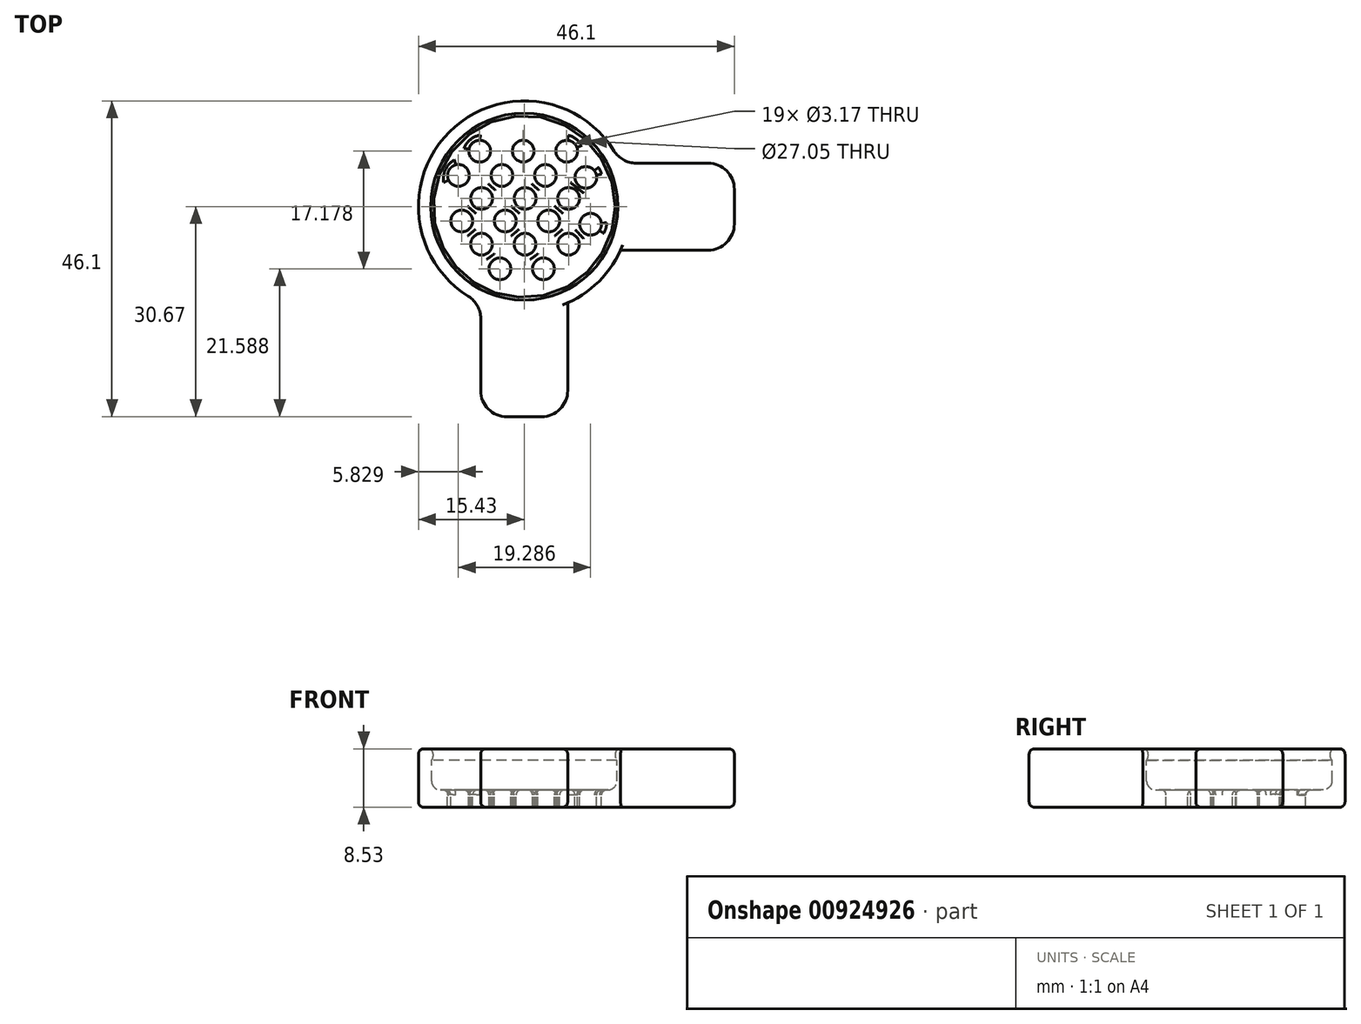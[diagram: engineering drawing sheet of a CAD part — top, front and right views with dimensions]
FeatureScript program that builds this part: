
annotation { "Feature Type Name" : "Feature", "Feature Type Description" : "" }
export const myFeature = defineFeature(function(context is Context, id is Id, definition is map)
    precondition{}
    {
        {
            var Q0;
            Q0=qCreatedBy(makeId("Front.planeOp"),FACE);
            var sketch = newSketch(context, id + "F0", { "sketchPlane" : qUnion([Q0])});
            skLineSegment(sketch, "E0", {"start": v(15.43, 6.71) * mm, "end": v(15.43, 0) * mm});
            skLineSegment(sketch, "E1", {"start": v(15.43, 0) * mm, "end": v(0, 0) * mm});
            skArc(sketch, "E2", {"start": v(15.43, 6.71) * mm, "mid": v(13.63, 6.73) * mm, "end": v(13.65, 8.53) * mm});
            skLineSegment(sketch, "E3", {"start": v(0, 10.9) * mm, "end": v(0, -2.45) * mm, "construction": true});
            skLineSegment(sketch, "E4", {"start": v(0, 0) * mm, "end": v(0, 2.54) * mm});
            skLineSegment(sketch, "E5", {"start": v(0, 2.54) * mm, "end": v(12.26, 2.54) * mm});
            skLineSegment(sketch, "E6", {"start": v(13.53, 3.81) * mm, "end": v(13.53, 6.86) * mm});
            skLineSegment(sketch, "E7", {"start": v(15.43, 6.71) * mm, "end": v(15.43, 8.53) * mm});
            skLineSegment(sketch, "E8", {"start": v(15.43, 8.53) * mm, "end": v(13.65, 8.53) * mm});
            skPoint(sketch, "E9.visualSharp", {"position": v(13.53, 2.54) * mm});
            skArc(sketch, "E10.filletArc", {"start": v(12.26, 2.54) * mm, "mid": v(13.15, 2.91) * mm, "end": v(13.53, 3.81) * mm});
            skPoint(sketch, "E11.visualSharp", {"position": v(15.43, 0) * mm});
            skPoint(sketch, "E12.visualSharp", {"position": v(15.43, 8.53) * mm});
            skSolve(sketch);
        }
        {
            var Q0;
            Q0=qSketchRegion(id+"F0",true);
            var Q1;
            Q1=sQuery(id+"F0.wireOp",EDGE,"E3");
            revolve(context, id + "F1", {"surfaceOperationType" : NewSurfaceOperationType.NEW, "entities" : qUnion([Q0]), "axis" : qUnion([Q1]), "revolveType" : RevolveType.FULL});
        }
        {
            var Q0;
            Q0=makeQuery(id+"F1.opRevolve","SWEPT_FACE",FACE,{"disambiguationData":[OSD([sQuery(id+"F0.wireOp",EDGE,"E8")])]});
            var sketch = newSketch(context, id + "F2", { "sketchPlane" : qUnion([Q0])});
            skLineSegment(sketch, "E13.bottom", {"start": v(30.67, 6.35) * mm, "end": v(14.06, 6.35) * mm});
            skLineSegment(sketch, "E13.top", {"start": v(30.67, -6.35) * mm, "end": v(14.06, -6.35) * mm});
            skLineSegment(sketch, "E13.left", {"start": v(30.67, 6.35) * mm, "end": v(30.67, -6.35) * mm});
            skLineSegment(sketch, "E14.bottom", {"start": v(6.35, -30.67) * mm, "end": v(-6.35, -30.67) * mm});
            skLineSegment(sketch, "E14.left", {"start": v(6.35, -30.67) * mm, "end": v(6.35, -14.06) * mm});
            skLineSegment(sketch, "E14.right", {"start": v(-6.35, -30.67) * mm, "end": v(-6.35, -14.06) * mm});
            skArc(sketch, "E15.0", {"start": v(-6.35, -14.06) * mm, "mid": v(0, -15.43) * mm, "end": v(6.35, -14.06) * mm});
            skArc(sketch, "E16.trimOffspring", {"start": v(14.06, -6.35) * mm, "mid": v(15.43, 0) * mm, "end": v(14.06, 6.35) * mm});
            skSolve(sketch);
        }
        {
            var Q0;
            Q0=qSketchRegion(id+"F2",true);
            var Q1;
            Q1=makeQuery(id+"F1.opRevolve","SWEPT_FACE",FACE,{"disambiguationData":[OSD([sQuery(id+"F0.wireOp",EDGE,"E1")])]});
            extrude(context, id + "F3", {"entities" : qUnion([Q0]), "operationType" : NewBodyOperationType.ADD, "endBound" : BoundingType.UP_TO_SURFACE, "oppositeDirection" : true, "depth" : 25.4 * mm, "endBoundEntityFace" : qUnion([Q1]), "offsetDistance" : 25.4 * mm});
        }
        {
            var Q0;
            Q0=makeQuery(id+"F3.opExtrude","SWEPT_EDGE",EDGE,{"disambiguationData":[OSD([sQuery(id+"F2.wireOp",EDGE,"E14.bottom"),sQuery(id+"F2.wireOp",EDGE,"E14.right")])]});
            var Q1;
            Q1=makeQuery(id+"F3.opExtrude","SWEPT_EDGE",EDGE,{"disambiguationData":[OSD([sQuery(id+"F0.wireOp",EDGE,"E7"),sQuery(id+"F0.wireOp",EDGE,"E8"),sQuery(id+"F2.wireOp",EDGE,"E14.right"),sQuery(id+"F2.wireOp",EDGE,"E15.0")])]});
            var Q2;
            Q2=makeQuery(id+"F3.opExtrude","SWEPT_EDGE",EDGE,{"disambiguationData":[OSD([sQuery(id+"F2.wireOp",EDGE,"E14.bottom"),sQuery(id+"F2.wireOp",EDGE,"E14.left")])]});
            var Q3;
            Q3=makeQuery(id+"F3.opExtrude","SWEPT_EDGE",EDGE,{"disambiguationData":[OSD([sQuery(id+"F0.wireOp",EDGE,"E7"),sQuery(id+"F0.wireOp",EDGE,"E8"),sQuery(id+"F2.wireOp",EDGE,"E14.left"),sQuery(id+"F2.wireOp",EDGE,"E15.0")])]});
            var Q4;
            Q4=makeQuery(id+"F3.opExtrude","SWEPT_EDGE",EDGE,{"disambiguationData":[OSD([sQuery(id+"F0.wireOp",EDGE,"E7"),sQuery(id+"F0.wireOp",EDGE,"E8"),sQuery(id+"F2.wireOp",EDGE,"E13.top"),sQuery(id+"F2.wireOp",EDGE,"E16.trimOffspring")])]});
            var Q5;
            Q5=makeQuery(id+"F3.opExtrude","SWEPT_EDGE",EDGE,{"disambiguationData":[OSD([sQuery(id+"F2.wireOp",EDGE,"E13.top"),sQuery(id+"F2.wireOp",EDGE,"E13.left")])]});
            var Q6;
            Q6=makeQuery(id+"F3.opExtrude","SWEPT_EDGE",EDGE,{"disambiguationData":[OSD([sQuery(id+"F2.wireOp",EDGE,"E13.bottom"),sQuery(id+"F2.wireOp",EDGE,"E13.left")])]});
            var Q7;
            Q7=makeQuery(id+"F3.opExtrude","SWEPT_EDGE",EDGE,{"disambiguationData":[OSD([sQuery(id+"F0.wireOp",EDGE,"E7"),sQuery(id+"F0.wireOp",EDGE,"E8"),sQuery(id+"F2.wireOp",EDGE,"E13.bottom"),sQuery(id+"F2.wireOp",EDGE,"E16.trimOffspring")])]});
            fillet(context, id + "F4", {"entities" : qUnion([Q0, Q1, Q2, Q3, Q4, Q5, Q6, Q7]), "radius" : 3.8 * mm, "tangentPropagation" : true, "allowEdgeOverflow" : false});
        }
        {
            var Q0;
            Q0=makeQuery(id+"F3.opExtrude","CAP_EDGE",EDGE,{"disambiguationData":[OSD([sQuery(id+"F2.wireOp",EDGE,"E14.bottom")])],"isStart":true});
            var Q1;
            Q1=makeQuery(id+"F3.opExtrude","CAP_EDGE",EDGE,{"disambiguationData":[OSD([sQuery(id+"F2.wireOp",EDGE,"E14.bottom")])],"isStart":false});
            fillet(context, id + "F5", {"entities" : qUnion([Q0, Q1]), "radius" : 0.76 * mm, "tangentPropagation" : true, "allowEdgeOverflow" : false});
        }
        {
            var Q0;
            Q0=makeQuery(id+"F1.opRevolve","SWEPT_FACE",FACE,{"disambiguationData":[OSD([sQuery(id+"F0.wireOp",EDGE,"E5")])]});
            var sketch = newSketch(context, id + "F6", { "sketchPlane" : qUnion([Q0])});
            skCircle(sketch, "E17", {"center": v(-6.7, 7.93) * mm, "radius": 1.4 * mm});
            skCircle(sketch, "E18.1.0.0", {"center": v(-2.25, 7.93) * mm, "radius": 1.4 * mm});
            skCircle(sketch, "E18.2.0.0", {"center": v(2.2, 7.93) * mm, "radius": 1.4 * mm});
            skCircle(sketch, "E18.3.0.0", {"center": v(6.64, 7.93) * mm, "radius": 1.4 * mm});
            skLineSegment(sketch, "E18.direction1", {"start": v(-6.7, 7.93) * mm, "end": v(-2.25, 7.93) * mm, "construction": true});
            skCircle(sketch, "E19", {"center": v(-8.66, 4.6) * mm, "radius": 1.4 * mm});
            skCircle(sketch, "E20.1.0.0", {"center": v(-4.22, 4.6) * mm, "radius": 1.4 * mm});
            skCircle(sketch, "E20.2.0.0", {"center": v(0.23, 4.6) * mm, "radius": 1.4 * mm});
            skCircle(sketch, "E20.3.0.0", {"center": v(4.67, 4.6) * mm, "radius": 1.4 * mm});
            skLineSegment(sketch, "E20.direction1", {"start": v(-8.66, 4.6) * mm, "end": v(-4.22, 4.6) * mm, "construction": true});
            skCircle(sketch, "E21.3.0.0", {"center": v(8.32, 4.74) * mm, "radius": 1.34 * mm});
            skCircle(sketch, "E22", {"center": v(-6.88, 1.46) * mm, "radius": 1.4 * mm});
            skCircle(sketch, "E23.1.0.0", {"center": v(-2.44, 1.46) * mm, "radius": 1.4 * mm});
            skCircle(sketch, "E23.2.0.0", {"center": v(2, 1.46) * mm, "radius": 1.4 * mm});
            skCircle(sketch, "E23.3.0.0", {"center": v(6.45, 1.46) * mm, "radius": 1.4 * mm});
            skLineSegment(sketch, "E23.direction1", {"start": v(-6.88, 1.46) * mm, "end": v(-2.44, 1.46) * mm, "construction": true});
            skCircle(sketch, "E24", {"center": v(-8.85, -1.87) * mm, "radius": 1.4 * mm});
            skCircle(sketch, "E25.1.0.0", {"center": v(-4.4, -1.87) * mm, "radius": 1.4 * mm});
            skCircle(sketch, "E25.2.0.0", {"center": v(0.04, -1.87) * mm, "radius": 1.4 * mm});
            skCircle(sketch, "E25.3.0.0", {"center": v(4.49, -1.87) * mm, "radius": 1.4 * mm});
            skLineSegment(sketch, "E25.direction1", {"start": v(-8.85, -1.87) * mm, "end": v(-4.4, -1.87) * mm, "construction": true});
            skCircle(sketch, "E26.3.0.0", {"center": v(8.13, -1.73) * mm, "radius": 1.34 * mm});
            skCircle(sketch, "E27", {"center": v(-6.6, -4.9) * mm, "radius": 1.4 * mm});
            skCircle(sketch, "E28.1.0.0", {"center": v(-2.16, -4.9) * mm, "radius": 1.4 * mm});
            skCircle(sketch, "E28.2.0.0", {"center": v(2.29, -4.9) * mm, "radius": 1.4 * mm});
            skCircle(sketch, "E28.3.0.0", {"center": v(6.73, -4.9) * mm, "radius": 1.4 * mm});
            skLineSegment(sketch, "E28.direction1", {"start": v(-6.6, -4.9) * mm, "end": v(-2.16, -4.9) * mm, "construction": true});
            skCircle(sketch, "E29", {"center": v(-4.25, -8.22) * mm, "radius": 1.4 * mm});
            skCircle(sketch, "E30.1.0.0", {"center": v(0.2, -8.22) * mm, "radius": 1.4 * mm});
            skCircle(sketch, "E30.2.0.0", {"center": v(4.64, -8.22) * mm, "radius": 1.4 * mm});
            skLineSegment(sketch, "E30.direction1", {"start": v(-4.25, -8.22) * mm, "end": v(0.2, -8.22) * mm, "construction": true});
            skSolve(sketch);
        }
        {
            var Q0;
            Q0=makeQuery(id+"F6.imprint","IMPRINT",FACE,{"disambiguationData":[TD([[makeQuery(id+"F6.imprint","IMPRINT",EDGE,{"derivedFrom":sQuery(id+"F6.wireOp",EDGE,"E17")}),-1.0]])]});
            var sketch = newSketch(context, id + "F7", { "sketchPlane" : qUnion([Q0])});
            skCircle(sketch, "E31", {"center": v(-6.5, 8.1) * mm, "radius": 1.59 * mm});
            skCircle(sketch, "E32.1.0.0", {"center": v(-0.14, 8.1) * mm, "radius": 1.59 * mm});
            skCircle(sketch, "E32.2.0.0", {"center": v(6.2, 8.1) * mm, "radius": 1.59 * mm});
            skLineSegment(sketch, "E32.direction1", {"start": v(-6.5, 8.1) * mm, "end": v(-0.14, 8.1) * mm, "construction": true});
            skCircle(sketch, "E33", {"center": v(-9.6, 4.55) * mm, "radius": 1.59 * mm});
            skCircle(sketch, "E34.1.0.0", {"center": v(-3.25, 4.55) * mm, "radius": 1.59 * mm});
            skCircle(sketch, "E34.2.0.0", {"center": v(3.1, 4.55) * mm, "radius": 1.59 * mm});
            skLineSegment(sketch, "E34.direction1", {"start": v(-9.6, 4.55) * mm, "end": v(-3.25, 4.55) * mm, "construction": true});
            skCircle(sketch, "E35", {"center": v(-6.22, 1.2) * mm, "radius": 1.59 * mm});
            skCircle(sketch, "E36.1.0.0", {"center": v(0.13, 1.2) * mm, "radius": 1.59 * mm});
            skCircle(sketch, "E36.2.0.0", {"center": v(6.48, 1.2) * mm, "radius": 1.59 * mm});
            skLineSegment(sketch, "E36.direction1", {"start": v(-6.22, 1.2) * mm, "end": v(0.13, 1.2) * mm, "construction": true});
            skCircle(sketch, "E37", {"center": v(-9.12, -2.1) * mm, "radius": 1.59 * mm});
            skCircle(sketch, "E38.1.0.0", {"center": v(-2.77, -2.1) * mm, "radius": 1.59 * mm});
            skCircle(sketch, "E38.2.0.0", {"center": v(3.58, -2.1) * mm, "radius": 1.59 * mm});
            skLineSegment(sketch, "E38.direction1", {"start": v(-9.12, -2.1) * mm, "end": v(-2.77, -2.1) * mm, "construction": true});
            skCircle(sketch, "E39", {"center": v(-6.24, -5.49) * mm, "radius": 1.59 * mm});
            skCircle(sketch, "E40.1.0.0", {"center": v(0.11, -5.49) * mm, "radius": 1.59 * mm});
            skCircle(sketch, "E40.2.0.0", {"center": v(6.46, -5.49) * mm, "radius": 1.59 * mm});
            skLineSegment(sketch, "E40.direction1", {"start": v(-6.24, -5.49) * mm, "end": v(0.11, -5.49) * mm, "construction": true});
            skCircle(sketch, "E41", {"center": v(-3.55, -9.08) * mm, "radius": 1.59 * mm});
            skCircle(sketch, "E42.1.0.0", {"center": v(2.8, -9.08) * mm, "radius": 1.59 * mm});
            skLineSegment(sketch, "E42.direction1", {"start": v(-3.55, -9.08) * mm, "end": v(2.8, -9.08) * mm, "construction": true});
            skCircle(sketch, "E43.2.0.0", {"center": v(9.69, -2.57) * mm, "radius": 1.59 * mm});
            skCircle(sketch, "E44.2.0.0", {"center": v(9, 4.26) * mm, "radius": 1.59 * mm});
            skSolve(sketch);
        }
        {
            var Q0;
            Q0 = qSketchRegion(id + "F7", true);
            extrude(context, id + "F8", {"entities" : qUnion([Q0]), "operationType" : NewBodyOperationType.REMOVE, "oppositeDirection" : true, "depth" : 25.4 * mm, "offsetDistance" : 25.4 * mm});
        }
        {
            var Q0;
            Q0=makeQuery(id+"F8.boolean.opBoolean","COPY",EDGE,{"derivedFrom":makeQuery(id+"F8.opExtrude","CAP_EDGE",EDGE,{"disambiguationData":[OSD([sQuery(id+"F7.wireOp",EDGE,"E33")])],"isStart":true})});
            var Q1;
            Q1=makeQuery(id+"F8.boolean.opBoolean","COPY",EDGE,{"derivedFrom":makeQuery(id+"F8.opExtrude","CAP_EDGE",EDGE,{"disambiguationData":[OSD([sQuery(id+"F7.wireOp",EDGE,"E31")])],"isStart":true})});
            var Q2;
            Q2=makeQuery(id+"F1.opRevolve","SWEPT_FACE",FACE,{"disambiguationData":[OSD([sQuery(id+"F0.wireOp",EDGE,"E5")])]});
            fillet(context, id + "F9", {"entities" : qUnion([Q0, Q1, Q2]), "radius" : 0.76 * mm, "tangentPropagation" : true, "allowEdgeOverflow" : false});
        }
    });
